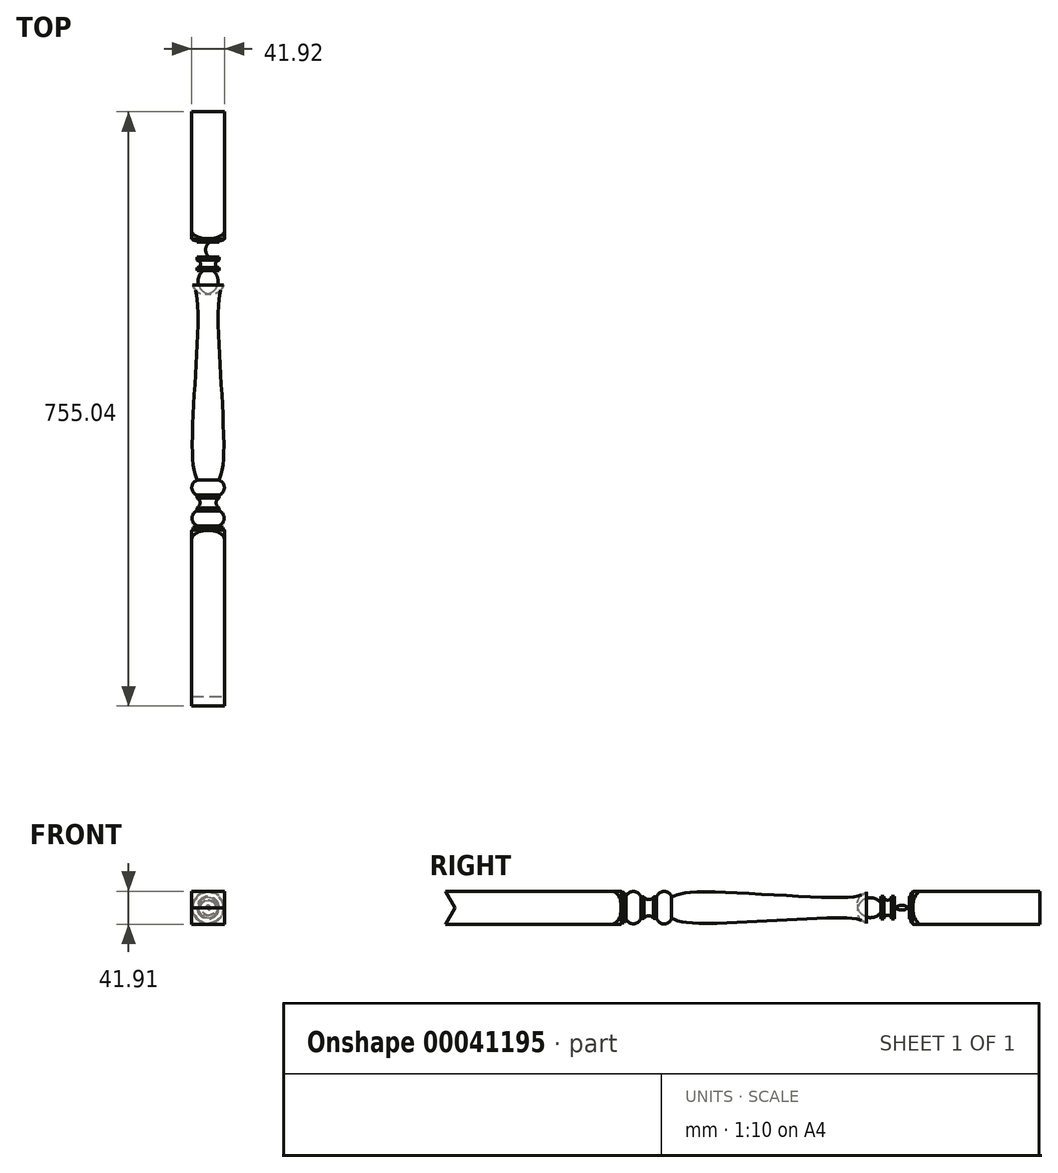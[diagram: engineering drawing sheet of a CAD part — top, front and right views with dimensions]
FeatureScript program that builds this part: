
annotation { "Feature Type Name" : "Feature", "Feature Type Description" : "" }
export const myFeature = defineFeature(function(context is Context, id is Id, definition is map)
    precondition{}
    {
        {
            var Q0;
            Q0=qCreatedBy(makeId("Right.planeOp"),FACE);
            var sketch = newSketch(context, id + "F0", { "sketchPlane" : qUnion([Q0])});
            skLineSegment(sketch, "E0", {"start": v(-278.65, 13.28) * mm, "end": v(-54.81, 13.28) * mm});
            skArc(sketch, "E1", {"start": v(-54.81, 13.28) * mm, "mid": v(-46.4, 16.2) * mm, "end": v(-41.6, 23.69) * mm});
            skLineSegment(sketch, "E2", {"start": v(-41.6, 23.69) * mm, "end": v(-38.43, 23.69) * mm});
            skLineSegment(sketch, "E3", {"start": v(-38.43, 23.69) * mm, "end": v(-36.14, 29.21) * mm});
            skArc(sketch, "E4", {"start": v(-36.14, 29.21) * mm, "mid": v(-26.62, 22.43) * mm, "end": v(-17.1, 29.21) * mm});
            skArc(sketch, "E5", {"start": v(-0.97, 29.21) * mm, "mid": v(-7.13, 32.71) * mm, "end": v(-13.28, 29.21) * mm});
            skLineSegment(sketch, "E6", {"start": v(-0.97, 29.21) * mm, "end": v(2.84, 29.21) * mm});
            skArc(sketch, "E7", {"start": v(2.84, 29.21) * mm, "mid": v(12.37, 22.22) * mm, "end": v(21.9, 29.21) * mm});
            skArc(sketch, "E8", {"start": v(269.35, 23.05) * mm, "mid": v(279.45, 22.93) * mm, "end": v(287.77, 28.64) * mm});
            skLineSegment(sketch, "E9", {"start": v(287.77, 28.64) * mm, "end": v(291.58, 28.64) * mm});
            skArc(sketch, "E10", {"start": v(301.1, 28.64) * mm, "mid": v(296.34, 33.4) * mm, "end": v(291.58, 28.64) * mm});
            skLineSegment(sketch, "E11", {"start": v(301.1, 28.64) * mm, "end": v(304.91, 28.64) * mm});
            skArc(sketch, "E12", {"start": v(304.91, 28.64) * mm, "mid": v(314.44, 23.44) * mm, "end": v(323.96, 28.64) * mm});
            skLineSegment(sketch, "E13", {"start": v(323.96, 28.64) * mm, "end": v(325.23, 28.64) * mm});
            skLineSegment(sketch, "E14", {"start": v(325.23, 28.64) * mm, "end": v(326.5, 23.69) * mm});
            skLineSegment(sketch, "E15", {"start": v(326.5, 23.69) * mm, "end": v(327.77, 23.69) * mm});
            skLineSegment(sketch, "E16", {"start": v(337.3, 13.28) * mm, "end": v(489.7, 13.28) * mm});
            skLineSegment(sketch, "E17", {"start": v(-278.65, 42.93) * mm, "end": v(610.35, 42.93) * mm, "construction": true});
            skLineSegment(sketch, "E18", {"start": v(-17.1, 29.21) * mm, "end": v(-13.28, 29.21) * mm});
            skArc(sketch, "E19", {"start": v(327.77, 23.69) * mm, "mid": v(331.37, 17.42) * mm, "end": v(337.3, 13.28) * mm});
            skLineSegment(sketch, "E20", {"start": v(38.25, 23.05) * mm, "end": v(191.9, 23.05) * mm, "construction": true});
            skFitSpline(sketch, "E21", {"points": [v(21.9, 29.21) * mm, v(52.9, 23.05) * mm, v(249.24, 29.61) * mm, v(269.35, 23.05) * mm], "startDerivative": vector(83.71, -33.8) * mm, "endDerivative": vector(63.68, -47.75) * mm});
            skLineSegment(sketch, "E22.0", {"start": v(-278.65, -33.84) * mm, "end": v(508.75, -33.84) * mm});
            skLineSegment(sketch, "E23", {"start": v(489.7, 13.28) * mm, "end": v(489.7, 42.93) * mm});
            skLineSegment(sketch, "E24", {"start": v(489.7, 42.93) * mm, "end": v(642.1, 42.93) * mm});
            skLineSegment(sketch, "E25", {"start": v(642.1, 42.93) * mm, "end": v(642.1, -33.84) * mm});
            skLineSegment(sketch, "E26", {"start": v(642.1, -33.84) * mm, "end": v(508.75, -33.84) * mm});
            skLineSegment(sketch, "E27", {"start": v(-278.65, 13.28) * mm, "end": v(-278.65, 42.93) * mm});
            skLineSegment(sketch, "E28", {"start": v(-278.65, 42.93) * mm, "end": v(-405.65, 42.93) * mm});
            skLineSegment(sketch, "E29", {"start": v(-405.65, 42.93) * mm, "end": v(-405.65, -33.84) * mm});
            skLineSegment(sketch, "E30", {"start": v(-405.65, -33.84) * mm, "end": v(-278.65, -33.84) * mm});
            skSolve(sketch);
        }
        {
            var Q0;
            Q0=qCreatedBy(makeId("Front.planeOp"),FACE);
            var sketch = newSketch(context, id + "F1", { "sketchPlane" : qUnion([Q0])});
            skPoint(sketch, "E31.0", {"position": v(0, 42.93) * mm});
            skLineSegment(sketch, "E32.0", {"start": v(-20.96, 21.98) * mm, "end": v(20.95, 21.98) * mm});
            skLineSegment(sketch, "E33.0", {"start": v(-20.96, 63.89) * mm, "end": v(20.95, 63.89) * mm});
            skLineSegment(sketch, "E34.0", {"start": v(20.95, 21.98) * mm, "end": v(20.95, 63.89) * mm});
            skLineSegment(sketch, "E35.0", {"start": v(-20.96, 21.98) * mm, "end": v(-20.96, 63.89) * mm});
            skSolve(sketch);
        }
        {
            var Q0;
            Q0=makeQuery(id+"F1.imprint","IMPRINT",FACE,{"disambiguationData":[TD([[makeQuery(id+"F1.imprint","IMPRINT",EDGE,{"derivedFrom":sQuery(id+"F1.wireOp",EDGE,"E32.0")}),1.0]])]});
            extrude(context, id + "F2", {"entities" : qUnion([Q0]), "depth" : 329.3 * mm});
        }
        {
            var Q0;
            Q0=makeQuery(id+"F2.opExtrude","CAP_FACE",FACE,{"disambiguationData":[OSD([sQuery(id+"F1.wireOp",EDGE,"E32.0"),sQuery(id+"F1.wireOp",EDGE,"E33.0"),sQuery(id+"F1.wireOp",EDGE,"E34.0"),sQuery(id+"F1.wireOp",EDGE,"E35.0")])],"isStart":true});
            extrude(context, id + "F3", {"entities" : qUnion([Q0]), "operationType" : NewBodyOperationType.ADD, "depth" : 569.35 * mm});
        }
        {
            var Q0;
            Q0=makeQuery(id+"F0.imprint","IMPRINT",FACE,{"disambiguationData":[TD([[makeQuery(id+"F0.imprint","IMPRINT",EDGE,{"derivedFrom":sQuery(id+"F0.wireOp",EDGE,"E0")}),-1.0]])]});
            var Q1;
            Q1=sQuery(id+"F0.wireOp",EDGE,"E17");
            revolve(context, id + "F4", {"operationType" : NewBodyOperationType.REMOVE, "entities" : qUnion([Q0]), "axis" : qUnion([Q1]), "revolveType" : RevolveType.FULL, "oppositeDirection" : true});
        }
        {
            var Q0;
            {var subQ0=sQuery(id+"F1.wireOp",EDGE,"E34.0");Q0=makeQuery(id+"F4.boolean.opBoolean","SPLIT",FACE,{"disambiguationData":[TD([makeQuery(id+"F4.opRevolve","SWEPT_FACE",FACE,{"disambiguationData":[OSD([sQuery(id+"F0.wireOp",EDGE,"E1")])]})])],"derivedFrom":makeQuery(id+"F3.boolean.opBoolean","MERGE",FACE,{"derivedFrom":[makeQuery(id+"F2.opExtrude","SWEPT_FACE",FACE,{"disambiguationData":[OSD([subQ0])]}),makeQuery(id+"F3.opExtrude","SWEPT_FACE",FACE,{"disambiguationData":[OSD([subQ0])]})]})});}
            var sketch = newSketch(context, id + "F5", { "sketchPlane" : qUnion([Q0])});
            skLineSegment(sketch, "E36", {"start": v(-278.65, 63.89) * mm, "end": v(-278.65, 21.98) * mm});
            skLineSegment(sketch, "E37", {"start": v(-278.65, 63.89) * mm, "end": v(-265.34, 63.89) * mm});
            skLineSegment(sketch, "E38", {"start": v(-278.65, 21.98) * mm, "end": v(-265.34, 21.98) * mm});
            skLineSegment(sketch, "E39", {"start": v(-265.34, 21.98) * mm, "end": v(-253.24, 42.93) * mm});
            skLineSegment(sketch, "E40", {"start": v(-253.24, 42.93) * mm, "end": v(-265.34, 63.89) * mm});
            skSolve(sketch);
        }
        {
            var Q0;
            Q0=makeQuery(id+"F5.imprint","IMPRINT",FACE,{"disambiguationData":[TD([[makeQuery(id+"F5.imprint","IMPRINT",EDGE,{"derivedFrom":sQuery(id+"F5.wireOp",EDGE,"E36")}),-1.0]])]});
            extrude(context, id + "F6", {"entities" : qUnion([Q0]), "operationType" : NewBodyOperationType.REMOVE, "oppositeDirection" : true, "depth" : 43.18 * mm});
        }
    });
